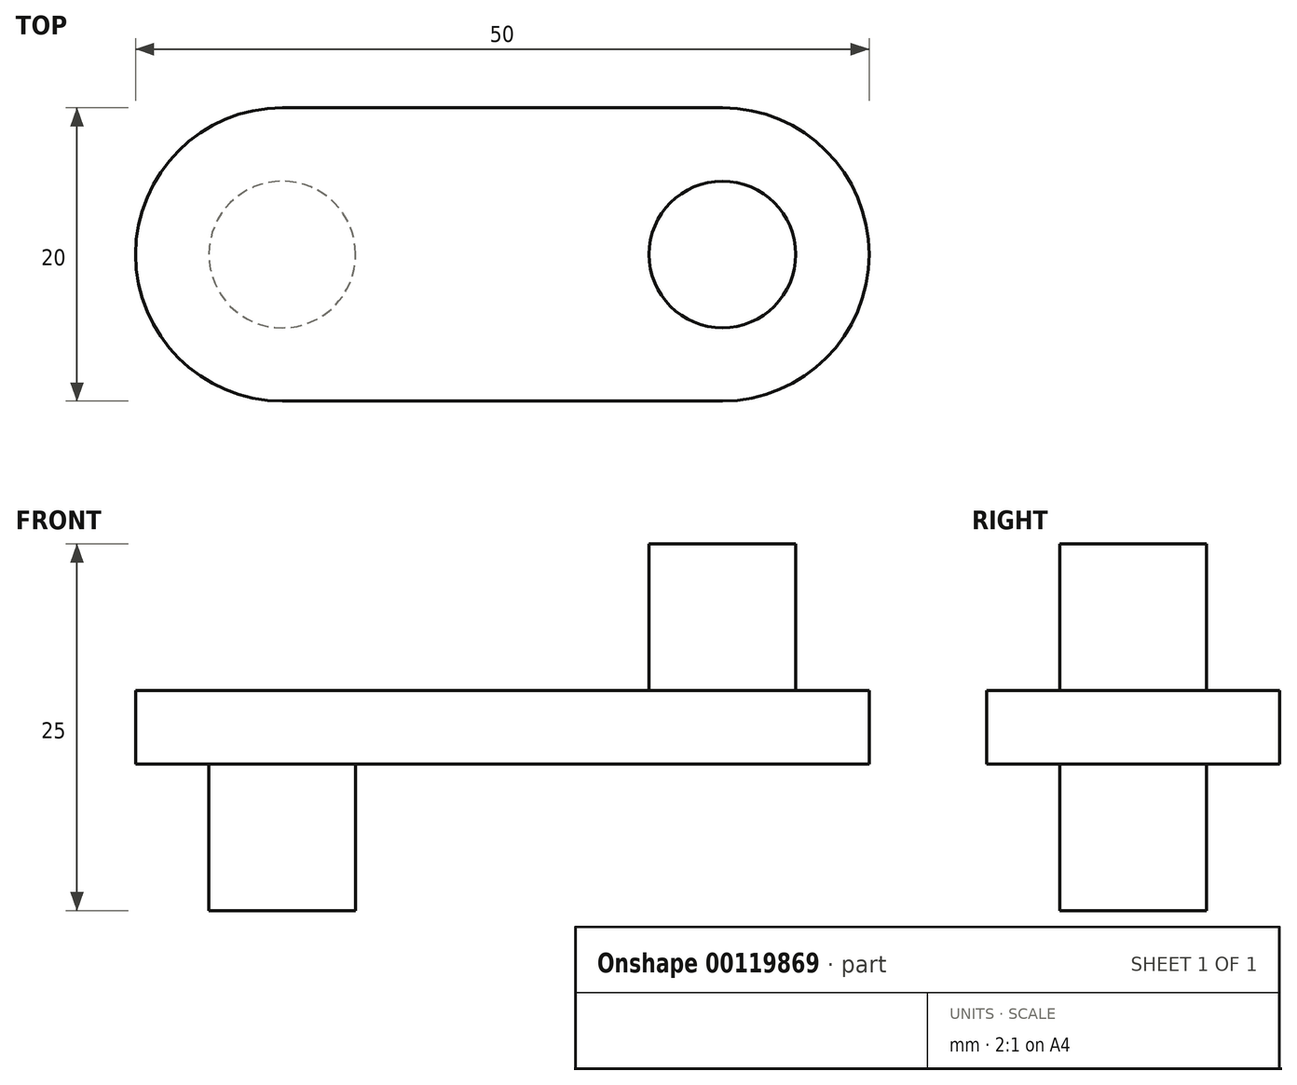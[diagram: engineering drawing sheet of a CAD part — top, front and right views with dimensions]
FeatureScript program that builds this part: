
annotation { "Feature Type Name" : "Feature", "Feature Type Description" : "" }
export const myFeature = defineFeature(function(context is Context, id is Id, definition is map)
    precondition{}
    {
        {
            var Q0;
            Q0=qCreatedBy(makeId("Top.planeOp"),FACE);
            var sketch = newSketch(context, id + "F0", { "sketchPlane" : qUnion([Q0])});
            skLineSegment(sketch, "E0", {"start": v(0, 0) * mm, "end": v(0, 20) * mm, "construction": true});
            skLineSegment(sketch, "E1", {"start": v(0, 20) * mm, "end": v(30, 20) * mm, "construction": true});
            skLineSegment(sketch, "E2", {"start": v(30, 20) * mm, "end": v(30, 0) * mm, "construction": true});
            skLineSegment(sketch, "E3", {"start": v(30, 0) * mm, "end": v(0, 0) * mm, "construction": true});
            skArc(sketch, "E4", {"start": v(0, 20) * mm, "mid": v(-10, 10) * mm, "end": v(0, 0) * mm});
            skArc(sketch, "E5", {"start": v(30, 0) * mm, "mid": v(40, 10) * mm, "end": v(30, 20) * mm});
            skLineSegment(sketch, "E6", {"start": v(0, 20) * mm, "end": v(30, 20) * mm});
            skLineSegment(sketch, "E7", {"start": v(30, 0) * mm, "end": v(0, 0) * mm});
            skSolve(sketch);
        }
        {
            var Q0;
            Q0=makeQuery(id+"F0.imprint","IMPRINT",FACE,{"disambiguationData":[TD([[makeQuery(id+"F0.imprint","IMPRINT",EDGE,{"derivedFrom":sQuery(id+"F0.wireOp",EDGE,"E4")}),1.0]])]});
            extrude(context, id + "F1", {"entities" : qUnion([Q0]), "depth" : 5 * mm});
        }
        {
            var Q0;
            Q0=makeQuery(id+"F1.opExtrude","CAP_FACE",FACE,{"disambiguationData":[OSD([sQuery(id+"F0.wireOp",EDGE,"E4"),sQuery(id+"F0.wireOp",EDGE,"E5"),sQuery(id+"F0.wireOp",EDGE,"E6"),sQuery(id+"F0.wireOp",EDGE,"E7")])],"isStart":false});
            var sketch = newSketch(context, id + "F2", { "sketchPlane" : qUnion([Q0])});
            skLineSegment(sketch, "E8", {"start": v(0, 0) * mm, "end": v(0, 10) * mm, "construction": true});
            skLineSegment(sketch, "E9", {"start": v(0, 10) * mm, "end": v(30, 10) * mm, "construction": true});
            skCircle(sketch, "E10", {"center": v(30, 10) * mm, "radius": 5 * mm});
            skSolve(sketch);
        }
        {
            var Q0;
            Q0=makeQuery(id+"F2.imprint","IMPRINT",FACE,{"disambiguationData":[TD([[makeQuery(id+"F2.imprint","IMPRINT",EDGE,{"derivedFrom":sQuery(id+"F2.wireOp",EDGE,"E10")}),1.0]])]});
            var Q1;
            Q1=sQuery(id+"F2.wireOp",EDGE,"E10");
            extrude(context, id + "F3", {"entities" : qUnion([Q0]), "operationType" : NewBodyOperationType.ADD, "surfaceEntities" : qUnion([Q1]), "depth" : 10 * mm});
        }
        {
            var Q0;
            Q0=makeQuery(id+"F1.opExtrude","CAP_FACE",FACE,{"disambiguationData":[OSD([sQuery(id+"F0.wireOp",EDGE,"E4"),sQuery(id+"F0.wireOp",EDGE,"E5"),sQuery(id+"F0.wireOp",EDGE,"E6"),sQuery(id+"F0.wireOp",EDGE,"E7")])],"isStart":true});
            var sketch = newSketch(context, id + "F4", { "sketchPlane" : qUnion([Q0])});
            skLineSegment(sketch, "E11", {"start": v(0, 0) * mm, "end": v(0, -10) * mm, "construction": true});
            skCircle(sketch, "E12", {"center": v(0, -10) * mm, "radius": 5 * mm});
            skSolve(sketch);
        }
        {
            var Q0;
            Q0=makeQuery(id+"F4.imprint","IMPRINT",FACE,{"disambiguationData":[TD([[makeQuery(id+"F4.imprint","IMPRINT",EDGE,{"derivedFrom":sQuery(id+"F4.wireOp",EDGE,"E12")}),1.0]])]});
            var Q1;
            Q1=sQuery(id+"F4.wireOp",EDGE,"E12");
            extrude(context, id + "F5", {"entities" : qUnion([Q0]), "operationType" : NewBodyOperationType.ADD, "surfaceEntities" : qUnion([Q1]), "depth" : 10 * mm});
        }
    });
